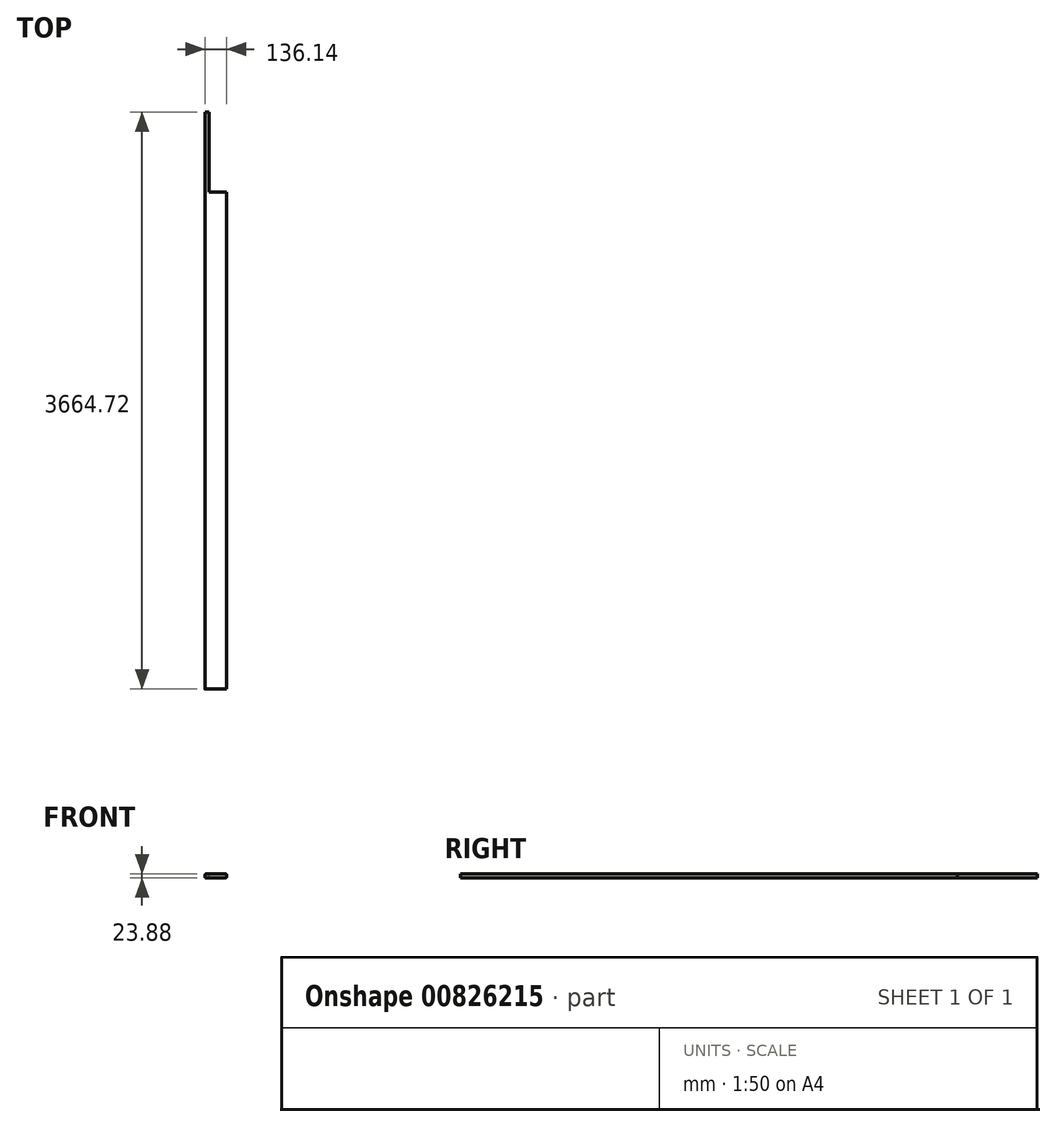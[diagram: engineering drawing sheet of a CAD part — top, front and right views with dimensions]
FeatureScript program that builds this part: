
annotation { "Feature Type Name" : "Feature", "Feature Type Description" : "" }
export const myFeature = defineFeature(function(context is Context, id is Id, definition is map)
    precondition{}
    {
        {
            var Q0;
            Q0=qCreatedBy(makeId("Front.planeOp"),FACE);
            var sketch = newSketch(context, id + "F0", { "sketchPlane" : qUnion([Q0])});
            skLineSegment(sketch, "E0.bottom", {"start": v(-63.25, 11.94) * mm, "end": v(63.25, 11.94) * mm});
            skLineSegment(sketch, "E0.top", {"start": v(-63.25, -11.94) * mm, "end": v(63.25, -11.94) * mm});
            skLineSegment(sketch, "E0.left", {"start": v(-68.07, 7.11) * mm, "end": v(-68.07, -7.11) * mm});
            skLineSegment(sketch, "E0.right", {"start": v(68.07, 7.11) * mm, "end": v(68.07, -7.11) * mm});
            skPoint(sketch, "E0.middle", {"position": v(0, 0) * mm});
            skPoint(sketch, "E1.visualSharp", {"position": v(-68.07, 11.94) * mm});
            skArc(sketch, "E1.filletArc", {"start": v(-63.25, 11.94) * mm, "mid": v(-66.66, 10.52) * mm, "end": v(-68.07, 7.11) * mm});
            skPoint(sketch, "E2.visualSharp", {"position": v(68.07, 11.94) * mm});
            skArc(sketch, "E2.filletArc", {"start": v(68.07, 7.11) * mm, "mid": v(66.66, 10.52) * mm, "end": v(63.25, 11.94) * mm});
            skPoint(sketch, "E3.visualSharp", {"position": v(68.07, -11.94) * mm});
            skArc(sketch, "E3.filletArc", {"start": v(63.25, -11.94) * mm, "mid": v(66.66, -10.52) * mm, "end": v(68.07, -7.11) * mm});
            skPoint(sketch, "E4.visualSharp", {"position": v(-68.07, -11.94) * mm});
            skArc(sketch, "E4.filletArc", {"start": v(-68.07, -7.11) * mm, "mid": v(-66.66, -10.52) * mm, "end": v(-63.25, -11.94) * mm});
            skSolve(sketch);
        }
        {
            var Q0;
            Q0=makeQuery(id+"F0.imprint","IMPRINT",FACE,{"disambiguationData":[TD([[makeQuery(id+"F0.imprint","IMPRINT",EDGE,{"derivedFrom":sQuery(id+"F0.wireOp",EDGE,"E0.bottom")}),-1.0]])]});
            extrude(context, id + "F1", {"entities" : qUnion([Q0]), "endBound" : BoundingType.SYMMETRIC, "depth" : 3664.71 * mm, "offsetDistance" : 25.4 * mm});
        }
        {
            var Q0;
            Q0=makeQuery(id+"F1.opExtrude","SWEPT_FACE",FACE,{"disambiguationData":[OSD([sQuery(id+"F0.wireOp",EDGE,"E0.bottom")])]});
            var sketch = newSketch(context, id + "F2", { "sketchPlane" : qUnion([Q0])});
            skLineSegment(sketch, "E5.bottom", {"start": v(68.07, 1832.36) * mm, "end": v(-42.55, 1832.36) * mm});
            skLineSegment(sketch, "E5.left", {"start": v(68.07, 1832.36) * mm, "end": v(68.07, 1324.36) * mm});
            skLineSegment(sketch, "E5.right", {"start": v(-42.55, 1832.36) * mm, "end": v(-42.55, 1324.36) * mm});
            skLineSegment(sketch, "E6", {"start": v(68.07, 1324.36) * mm, "end": v(-42.55, 1324.36) * mm});
            skSolve(sketch);
        }
        {
            var Q0;
            Q0=qSketchRegion(id+"F2",true);
            extrude(context, id + "F3", {"entities" : qUnion([Q0]), "operationType" : NewBodyOperationType.REMOVE, "endBound" : BoundingType.THROUGH_ALL, "oppositeDirection" : true, "depth" : 25.4 * mm, "offsetDistance" : 25.4 * mm});
        }
    });
